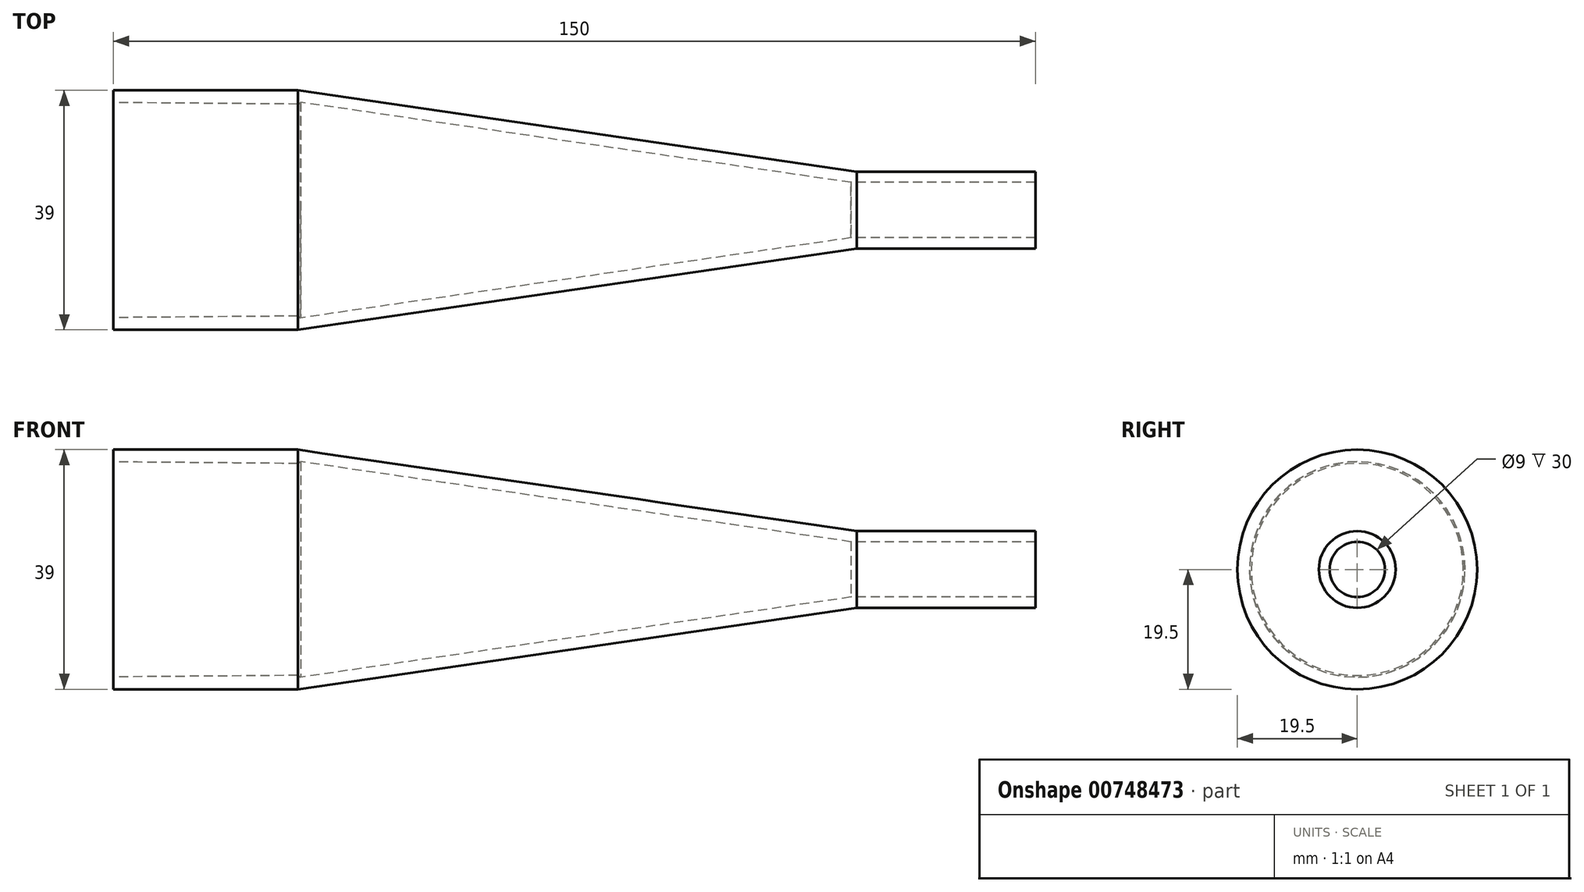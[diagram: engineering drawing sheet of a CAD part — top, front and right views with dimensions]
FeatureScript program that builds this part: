
annotation { "Feature Type Name" : "Feature", "Feature Type Description" : "" }
export const myFeature = defineFeature(function(context is Context, id is Id, definition is map)
    precondition{}
    {
        {
            var Q0;
            Q0=qCreatedBy(makeId("Front.planeOp"),FACE);
            var sketch = newSketch(context, id + "F0", { "sketchPlane" : qUnion([Q0])});
            skLineSegment(sketch, "E0", {"start": v(-46.46, 0) * mm, "end": v(46.11, 0) * mm, "construction": true});
            skLineSegment(sketch, "E1", {"start": v(0, 0) * mm, "end": v(0, 17.5) * mm, "construction": true});
            skLineSegment(sketch, "E2", {"start": v(30, 0) * mm, "end": v(30, 17.25) * mm, "construction": true});
            skLineSegment(sketch, "E3", {"start": v(150, 0) * mm, "end": v(150, 4.5) * mm, "construction": true});
            skLineSegment(sketch, "E4", {"start": v(0, 17.5) * mm, "end": v(30, 17.25) * mm});
            skLineSegment(sketch, "E5", {"start": v(150, 0) * mm, "end": v(120, 0) * mm, "construction": true});
            skLineSegment(sketch, "E6", {"start": v(30.43, 17.55) * mm, "end": v(120, 4.5) * mm});
            skLineSegment(sketch, "E7", {"start": v(120, 4.5) * mm, "end": v(150, 4.5) * mm});
            skLineSegment(sketch, "E8", {"start": v(150, 4.5) * mm, "end": v(150, 6.25) * mm});
            skLineSegment(sketch, "E9", {"start": v(150, 6.25) * mm, "end": v(120.97, 6.25) * mm});
            skLineSegment(sketch, "E10", {"start": v(120.97, 6.25) * mm, "end": v(30, 19.5) * mm});
            skLineSegment(sketch, "E11", {"start": v(30, 19.5) * mm, "end": v(0, 19.5) * mm});
            skLineSegment(sketch, "E12", {"start": v(0, 19.5) * mm, "end": v(0, 17.5) * mm});
            skLineSegment(sketch, "E13", {"start": v(30, 17.25) * mm, "end": v(30.43, 17.55) * mm});
            skSolve(sketch);
        }
        {
            var Q0;
            Q0 = qSketchRegion(id + "F0", true);
            var Q1;
            Q1=sQuery(id+"F0.wireOp",EDGE,"E0");
            revolve(context, id + "F1", {"surfaceOperationType" : NewSurfaceOperationType.NEW, "entities" : qUnion([Q0]), "axis" : qUnion([Q1]), "revolveType" : RevolveType.FULL});
        }
    });
